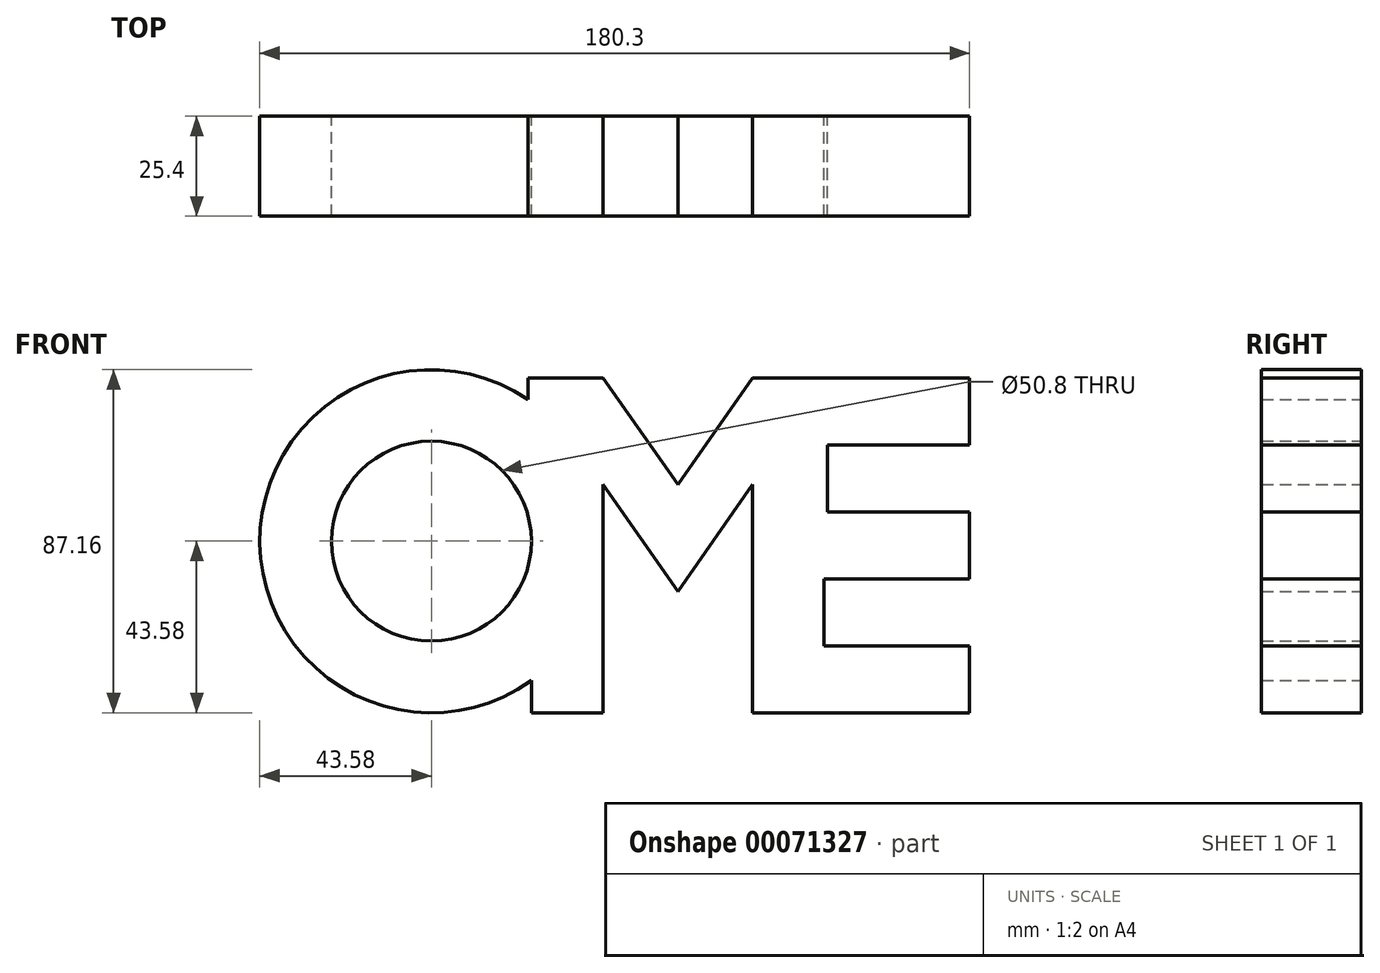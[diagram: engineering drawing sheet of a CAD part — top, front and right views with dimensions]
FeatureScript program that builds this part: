
annotation { "Feature Type Name" : "Feature", "Feature Type Description" : "" }
export const myFeature = defineFeature(function(context is Context, id is Id, definition is map)
    precondition{}
    {
        {
            var Q0;
            Q0=qCreatedBy(makeId("Front.planeOp"),FACE);
            var sketch = newSketch(context, id + "F0", { "sketchPlane" : qUnion([Q0])});
            skArc(sketch, "E0", {"start": v(24.53, 36.02) * mm, "mid": v(-43.58, -0.53) * mm, "end": v(25.4, -35.41) * mm});
            skCircle(sketch, "E1", {"center": v(0, 0) * mm, "radius": 25.4 * mm});
            skLineSegment(sketch, "E2.top", {"start": v(25.4, -43.58) * mm, "end": v(43.59, -43.58) * mm});
            skLineSegment(sketch, "E2.left", {"start": v(25.4, -35.41) * mm, "end": v(25.4, -43.58) * mm});
            skLineSegment(sketch, "E2.right", {"start": v(43.59, 0) * mm, "end": v(43.59, -43.58) * mm});
            skLineSegment(sketch, "E3.MirrorCS", {"start": v(43.58, 0) * mm, "end": v(43.58, 14.36) * mm});
            skLineSegment(sketch, "E4.MirrorCS", {"start": v(24.53, 41.5) * mm, "end": v(43.58, 41.5) * mm});
            skLineSegment(sketch, "E5.MirrorCS", {"start": v(24.53, 36.02) * mm, "end": v(24.53, 41.5) * mm});
            skLineSegment(sketch, "E6", {"start": v(62.6, 42.6) * mm, "end": v(62.6, 41.5) * mm});
            skLineSegment(sketch, "E7.MirrorCS", {"start": v(81.63, 0) * mm, "end": v(81.63, 14.36) * mm});
            skLineSegment(sketch, "E8.MirrorCS", {"start": v(81.62, 0) * mm, "end": v(81.62, -43.58) * mm});
            skLineSegment(sketch, "E9.MirrorCS", {"start": v(99.81, -9.55) * mm, "end": v(99.81, -26.56) * mm});
            skLineSegment(sketch, "E10.MirrorCS", {"start": v(100.68, 7.47) * mm, "end": v(100.68, 24.5) * mm});
            skLineSegment(sketch, "E11", {"start": v(43.58, 14.36) * mm, "end": v(62.6, -12.75) * mm});
            skLineSegment(sketch, "E12", {"start": v(43.58, 41.5) * mm, "end": v(62.6, 14.4) * mm});
            skLineSegment(sketch, "E13", {"start": v(62.6, 14.4) * mm, "end": v(81.63, 41.5) * mm});
            skLineSegment(sketch, "E14", {"start": v(62.6, -12.75) * mm, "end": v(81.63, 14.36) * mm});
            skLineSegment(sketch, "E15.bottom", {"start": v(81.63, 41.5) * mm, "end": v(136.72, 41.5) * mm});
            skLineSegment(sketch, "E15.top", {"start": v(100.68, 24.5) * mm, "end": v(136.72, 24.5) * mm});
            skLineSegment(sketch, "E15.right", {"start": v(136.72, 41.5) * mm, "end": v(136.72, 24.5) * mm});
            skLineSegment(sketch, "E16.bottom", {"start": v(99.81, -26.56) * mm, "end": v(136.72, -26.56) * mm});
            skLineSegment(sketch, "E16.top", {"start": v(81.62, -43.58) * mm, "end": v(136.72, -43.58) * mm});
            skLineSegment(sketch, "E16.left", {"start": v(81.62, -26.56) * mm, "end": v(81.62, -43.58) * mm});
            skLineSegment(sketch, "E16.right", {"start": v(136.72, -26.56) * mm, "end": v(136.72, -43.58) * mm});
            skLineSegment(sketch, "E17.bottom", {"start": v(100.68, 7.47) * mm, "end": v(136.72, 7.47) * mm});
            skLineSegment(sketch, "E17.top", {"start": v(99.81, -9.55) * mm, "end": v(136.72, -9.55) * mm});
            skLineSegment(sketch, "E17.left", {"start": v(81.63, 7.47) * mm, "end": v(81.63, -9.55) * mm});
            skLineSegment(sketch, "E17.right", {"start": v(136.72, 7.47) * mm, "end": v(136.72, -9.55) * mm});
            skLineSegment(sketch, "E18.trimOffspring", {"start": v(43.58, 41.5) * mm, "end": v(43.58, 41.5) * mm});
            skPoint(sketch, "E2.bottom.start.orphan", {"position": v(25.4, 0) * mm});
            skPoint(sketch, "E19.orphan", {"position": v(0, -43.58) * mm});
            skLineSegment(sketch, "E20", {"start": v(43.58, 14.36) * mm, "end": v(43.59, -43.58) * mm});
            skLineSegment(sketch, "E21", {"start": v(81.63, 14.36) * mm, "end": v(81.62, -43.58) * mm});
            skSolve(sketch);
        }
        {
            var Q0;
            Q0=makeQuery(id+"F0.imprint","IMPRINT",FACE,{"disambiguationData":[TD([[makeQuery(id+"F0.imprint","IMPRINT",EDGE,{"derivedFrom":sQuery(id+"F0.wireOp",EDGE,"E0")}),1.0]])]});
            extrude(context, id + "F1", {"entities" : qUnion([Q0]), "depth" : 25.4 * mm});
        }
    });
